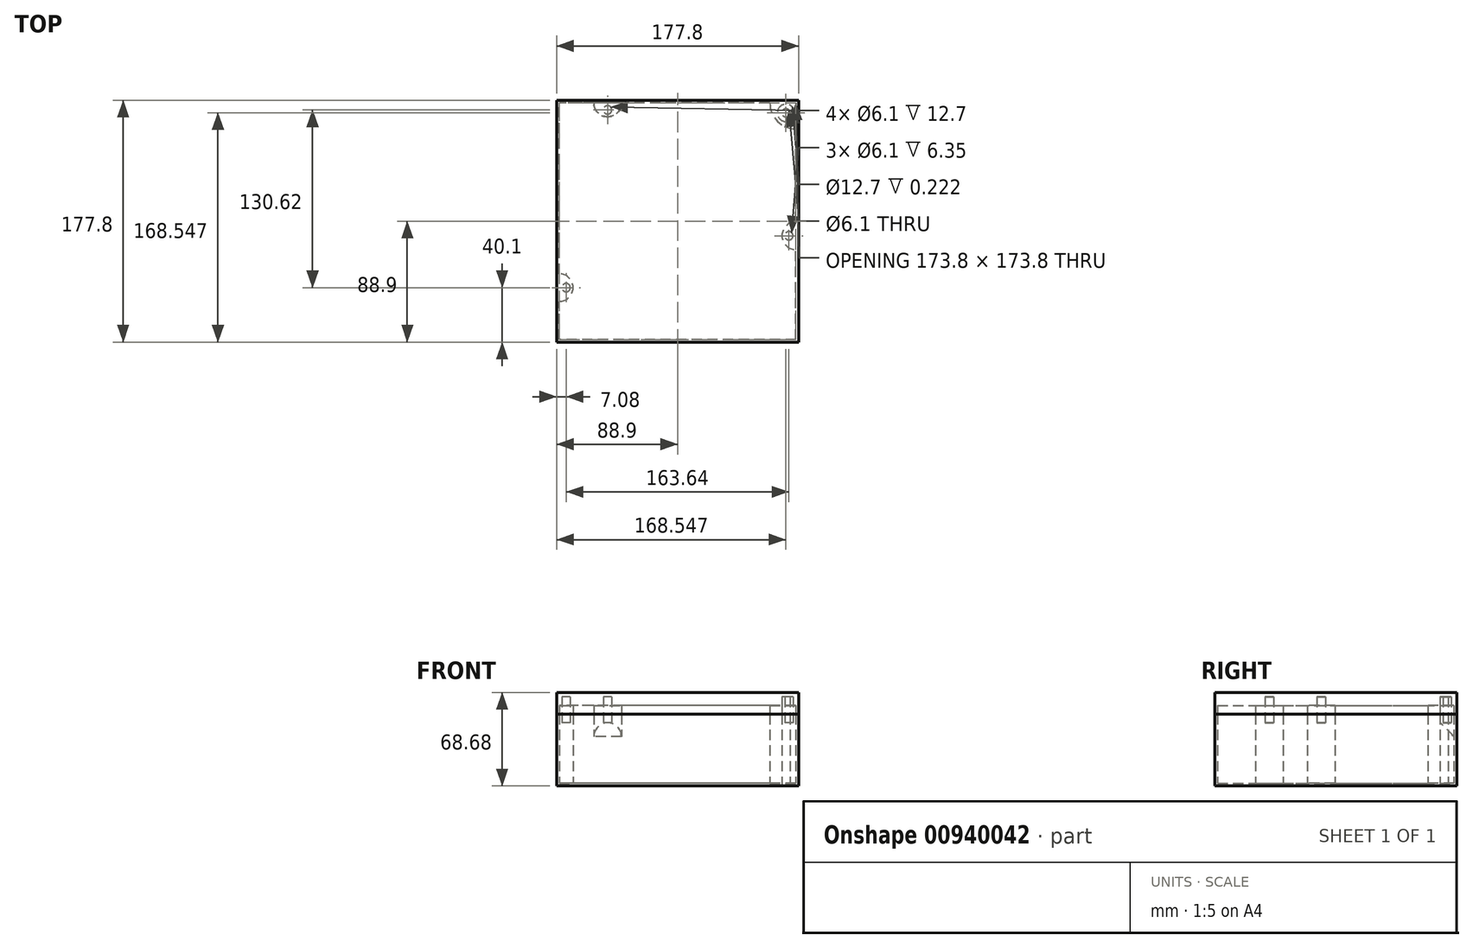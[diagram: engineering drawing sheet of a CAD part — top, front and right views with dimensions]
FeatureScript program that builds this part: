
annotation { "Feature Type Name" : "Feature", "Feature Type Description" : "" }
export const myFeature = defineFeature(function(context is Context, id is Id, definition is map)
    precondition{}
    {
        {
            var Q0;
            Q0=qCreatedBy(makeId("Top.planeOp"),FACE);
            var sketch = newSketch(context, id + "F0", { "sketchPlane" : qUnion([Q0])});
            skLineSegment(sketch, "E0.bottom", {"start": v(88.9, -88.9) * mm, "end": v(-88.9, -88.9) * mm});
            skLineSegment(sketch, "E0.top", {"start": v(88.9, 88.9) * mm, "end": v(-88.9, 88.9) * mm});
            skLineSegment(sketch, "E0.left", {"start": v(88.9, -88.9) * mm, "end": v(88.9, 88.9) * mm});
            skLineSegment(sketch, "E0.right", {"start": v(-88.9, -88.9) * mm, "end": v(-88.9, 88.9) * mm});
            skPoint(sketch, "E0.middle", {"position": v(0, 0) * mm});
            skSolve(sketch);
        }
        {
            var Q0;
            Q0=makeQuery(id+"F0.imprint","IMPRINT",FACE,{"disambiguationData":[TD([[makeQuery(id+"F0.imprint","IMPRINT",EDGE,{"derivedFrom":sQuery(id+"F0.wireOp",EDGE,"E0.bottom")}),-1.0]])]});
            extrude(context, id + "F1", {"entities" : qUnion([Q0]), "depth" : 6.35 * mm, "offsetDistance" : 25 * mm});
        }
        {
            var Q0;
            Q0=makeQuery(id+"F1.opExtrude","CAP_FACE",FACE,{"disambiguationData":[OSD([sQuery(id+"F0.wireOp",EDGE,"E0.bottom"),sQuery(id+"F0.wireOp",EDGE,"E0.top"),sQuery(id+"F0.wireOp",EDGE,"E0.left"),sQuery(id+"F0.wireOp",EDGE,"E0.right")])],"isStart":false});
            var sketch = newSketch(context, id + "F2", { "sketchPlane" : qUnion([Q0])});
            skLineSegment(sketch, "E1.bottom", {"start": v(86.9, -86.9) * mm, "end": v(-86.9, -86.9) * mm});
            skLineSegment(sketch, "E1.top", {"start": v(67.85, 86.9) * mm, "end": v(-41.18, 86.9) * mm});
            skLineSegment(sketch, "E1.left", {"start": v(86.9, -86.9) * mm, "end": v(86.9, -20.86) * mm});
            skLineSegment(sketch, "E1.right", {"start": v(-86.9, -86.9) * mm, "end": v(-86.9, -58.96) * mm});
            skPoint(sketch, "E1.middle", {"position": v(0, 0) * mm});
            skArc(sketch, "E2", {"start": v(-86.9, -58.96) * mm, "mid": v(-76.74, -48.8) * mm, "end": v(-86.9, -38.64) * mm});
            skArc(sketch, "E3", {"start": v(86.9, -0.54) * mm, "mid": v(76.74, -10.7) * mm, "end": v(86.9, -20.86) * mm});
            skArc(sketch, "E4", {"start": v(-61.5, 86.9) * mm, "mid": v(-51.34, 76.74) * mm, "end": v(-41.18, 86.9) * mm});
            skArc(sketch, "E5", {"start": v(67.85, 86.9) * mm, "mid": v(73.43, 73.43) * mm, "end": v(86.9, 67.85) * mm});
            skPoint(sketch, "E6.orphan", {"position": v(-51.34, 76.74) * mm});
            skLineSegment(sketch, "E7.trimOffspring", {"start": v(-61.5, 86.9) * mm, "end": v(-86.9, 86.9) * mm});
            skPoint(sketch, "E8.orphan", {"position": v(-76.74, -48.8) * mm});
            skLineSegment(sketch, "E9.trimOffspring", {"start": v(-86.9, -38.64) * mm, "end": v(-86.9, 86.9) * mm});
            skCircle(sketch, "E10", {"center": v(81.82, -10.7) * mm, "radius": 3.05 * mm});
            skLineSegment(sketch, "E11.trimOffspring", {"start": v(86.9, -0.54) * mm, "end": v(86.9, 67.85) * mm});
            skLineSegment(sketch, "E12", {"start": v(-86.9, 86.9) * mm, "end": v(-61.5, 86.9) * mm});
            skLineSegment(sketch, "E13.trimOffspring", {"start": v(-41.18, 86.9) * mm, "end": v(67.85, 86.9) * mm});
            skCircle(sketch, "E14", {"center": v(79.65, 79.65) * mm, "radius": 3.05 * mm});
            skLineSegment(sketch, "E15", {"start": v(86.9, -10.7) * mm, "end": v(76.74, -10.7) * mm});
            skCircle(sketch, "E16", {"center": v(-51.34, 81.82) * mm, "radius": 3.05 * mm});
            skCircle(sketch, "E17", {"center": v(-81.82, -48.8) * mm, "radius": 3.05 * mm});
            skPoint(sketch, "E18.start.orphan", {"position": v(88.9, 88.9) * mm});
            skSolve(sketch);
        }
        {
            var Q0;
            Q0=makeQuery(id+"F2.imprint","IMPRINT",FACE,{"disambiguationData":[TD([[makeQuery(id+"F2.imprint","IMPRINT",EDGE,{"derivedFrom":sQuery(id+"F2.wireOp",EDGE,"E1.bottom")}),1.0]])]});
            extrude(context, id + "F3", {"entities" : qUnion([Q0]), "operationType" : NewBodyOperationType.ADD, "depth" : 50.8 * mm, "offsetDistance" : 25.4 * mm});
        }
        {
            var Q0;
            Q0=makeQuery(id+"F3.boolean.opBoolean","SPLIT",FACE,{"disambiguationData":[TD([makeQuery(id+"F3.opExtrude","SWEPT_FACE",FACE,{"disambiguationData":[OSD([sQuery(id+"F2.wireOp",EDGE,"E16")])]})])],"derivedFrom":makeQuery(id+"F1.opExtrude","CAP_FACE",FACE,{"disambiguationData":[OSD([sQuery(id+"F0.wireOp",EDGE,"E0.bottom"),sQuery(id+"F0.wireOp",EDGE,"E0.top"),sQuery(id+"F0.wireOp",EDGE,"E0.left"),sQuery(id+"F0.wireOp",EDGE,"E0.right")])],"isStart":false})});
            var Q1;
            Q1=makeQuery(id+"F3.boolean.opBoolean","SPLIT",FACE,{"disambiguationData":[TD([makeQuery(id+"F3.opExtrude","SWEPT_FACE",FACE,{"disambiguationData":[OSD([sQuery(id+"F2.wireOp",EDGE,"E10")])]})])],"derivedFrom":makeQuery(id+"F1.opExtrude","CAP_FACE",FACE,{"disambiguationData":[OSD([sQuery(id+"F0.wireOp",EDGE,"E0.bottom"),sQuery(id+"F0.wireOp",EDGE,"E0.top"),sQuery(id+"F0.wireOp",EDGE,"E0.left"),sQuery(id+"F0.wireOp",EDGE,"E0.right")])],"isStart":false})});
            var Q2;
            Q2=makeQuery(id+"F3.boolean.opBoolean","SPLIT",FACE,{"disambiguationData":[TD([makeQuery(id+"F3.opExtrude","SWEPT_FACE",FACE,{"disambiguationData":[OSD([sQuery(id+"F2.wireOp",EDGE,"E17")])]})])],"derivedFrom":makeQuery(id+"F1.opExtrude","CAP_FACE",FACE,{"disambiguationData":[OSD([sQuery(id+"F0.wireOp",EDGE,"E0.bottom"),sQuery(id+"F0.wireOp",EDGE,"E0.top"),sQuery(id+"F0.wireOp",EDGE,"E0.left"),sQuery(id+"F0.wireOp",EDGE,"E0.right")])],"isStart":false})});
            extrude(context, id + "F4", {"entities" : qUnion([Q0, Q1, Q2]), "operationType" : NewBodyOperationType.ADD, "depth" : 44.45 * mm, "offsetDistance" : 25.4 * mm});
        }
        {
            var Q0;
            Q0=makeQuery(id+"F3.boolean.opBoolean","SPLIT",FACE,{"disambiguationData":[TD([makeQuery(id+"F3.opExtrude","SWEPT_FACE",FACE,{"disambiguationData":[OSD([sQuery(id+"F2.wireOp",EDGE,"E14")])]})])],"derivedFrom":makeQuery(id+"F1.opExtrude","CAP_FACE",FACE,{"disambiguationData":[OSD([sQuery(id+"F0.wireOp",EDGE,"E0.bottom"),sQuery(id+"F0.wireOp",EDGE,"E0.top"),sQuery(id+"F0.wireOp",EDGE,"E0.left"),sQuery(id+"F0.wireOp",EDGE,"E0.right")])],"isStart":false})});
            extrude(context, id + "F5", {"entities" : qUnion([Q0]), "operationType" : NewBodyOperationType.REMOVE, "oppositeDirection" : true, "depth" : 12.75 * mm, "offsetDistance" : 25.4 * mm});
        }
        {
            var Q0;
            Q0=makeQuery(id+"F1.opExtrude","CAP_FACE",FACE,{"disambiguationData":[OSD([sQuery(id+"F0.wireOp",EDGE,"E0.bottom"),sQuery(id+"F0.wireOp",EDGE,"E0.top"),sQuery(id+"F0.wireOp",EDGE,"E0.left"),sQuery(id+"F0.wireOp",EDGE,"E0.right")])],"isStart":true});
            var sketch = newSketch(context, id + "F6", { "sketchPlane" : qUnion([Q0])});
            skCircle(sketch, "E19", {"center": v(79.65, -79.65) * mm, "radius": 6.35 * mm});
            skSolve(sketch);
        }
        {
            var Q0;
            Q0=makeQuery(id+"F6.imprint","IMPRINT",FACE,{"disambiguationData":[TD([[makeQuery(id+"F6.imprint","IMPRINT",EDGE,{"derivedFrom":sQuery(id+"F6.wireOp",EDGE,"E19")}),1.0]])]});
            extrude(context, id + "F7", {"entities" : qUnion([Q0]), "operationType" : NewBodyOperationType.REMOVE, "oppositeDirection" : true, "depth" : 4.57 * mm, "offsetDistance" : 25.4 * mm});
        }
        {
            var Q0;
            Q0=makeQuery(id+"F3.opExtrude","CAP_FACE",FACE,{"disambiguationData":[OSD([sQuery(id+"F0.wireOp",EDGE,"E0.bottom"),sQuery(id+"F0.wireOp",EDGE,"E0.top"),sQuery(id+"F0.wireOp",EDGE,"E0.left"),sQuery(id+"F0.wireOp",EDGE,"E0.right"),sQuery(id+"F2.wireOp",EDGE,"E1.bottom"),sQuery(id+"F2.wireOp",EDGE,"E1.left"),sQuery(id+"F2.wireOp",EDGE,"E1.right"),sQuery(id+"F2.wireOp",EDGE,"E2"),sQuery(id+"F2.wireOp",EDGE,"E3"),sQuery(id+"F2.wireOp",EDGE,"E4"),sQuery(id+"F2.wireOp",EDGE,"E5"),sQuery(id+"F2.wireOp",EDGE,"SM7KM1Kk-73DD-m9rY-A4iJ-MEBE9odaTNSM"),sQuery(id+"F2.wireOp",EDGE,"twTWXflB-vlQ6-LPMN-hA2H-3E9qFKBzkKEc"),sQuery(id+"F2.wireOp",EDGE,"E9.trimOffspring"),sQuery(id+"F2.wireOp",EDGE,"E10"),sQuery(id+"F2.wireOp",EDGE,"E11.trimOffspring"),sQuery(id+"F2.wireOp",EDGE,"E12"),sQuery(id+"F2.wireOp",EDGE,"E13.trimOffspring"),sQuery(id+"F2.wireOp",EDGE,"E14")])],"isStart":false});
            var sketch = newSketch(context, id + "F8", { "sketchPlane" : qUnion([Q0])});
            skLineSegment(sketch, "E20.0.0", {"start": v(-88.9, -88.9) * mm, "end": v(88.9, -88.9) * mm});
            skLineSegment(sketch, "E20.0.1", {"start": v(88.9, -88.9) * mm, "end": v(88.9, 88.9) * mm});
            skLineSegment(sketch, "E20.0.2", {"start": v(88.9, 88.9) * mm, "end": v(-88.9, 88.9) * mm});
            skLineSegment(sketch, "E20.0.3", {"start": v(-88.9, 88.9) * mm, "end": v(-88.9, -88.9) * mm});
            skArc(sketch, "E21.0", {"start": v(-61.5, 86.9) * mm, "mid": v(-51.34, 76.74) * mm, "end": v(-41.18, 86.9) * mm});
            skArc(sketch, "E22.0.0", {"start": v(-41.18, 86.9) * mm, "mid": v(-51.34, 76.74) * mm, "end": v(-61.5, 86.9) * mm});
            skLineSegment(sketch, "E22.0.1", {"start": v(-61.5, 86.9) * mm, "end": v(-86.9, 86.9) * mm});
            skLineSegment(sketch, "E22.0.2", {"start": v(-86.9, 86.9) * mm, "end": v(-86.9, -38.64) * mm});
            skArc(sketch, "E22.0.3", {"start": v(-86.9, -38.64) * mm, "mid": v(-76.74, -48.8) * mm, "end": v(-86.9, -58.96) * mm});
            skLineSegment(sketch, "E22.0.4", {"start": v(-86.9, -58.96) * mm, "end": v(-86.9, -86.9) * mm});
            skLineSegment(sketch, "E22.0.5", {"start": v(-86.9, -86.9) * mm, "end": v(86.9, -86.9) * mm});
            skLineSegment(sketch, "E22.0.6", {"start": v(86.9, -86.9) * mm, "end": v(86.9, -20.86) * mm});
            skArc(sketch, "E22.0.7", {"start": v(86.9, -20.86) * mm, "mid": v(76.74, -10.7) * mm, "end": v(86.9, -0.54) * mm});
            skLineSegment(sketch, "E22.0.8", {"start": v(86.9, -0.54) * mm, "end": v(86.9, 67.85) * mm});
            skArc(sketch, "E22.0.9", {"start": v(86.9, 67.85) * mm, "mid": v(73.43, 73.43) * mm, "end": v(67.85, 86.9) * mm});
            skLineSegment(sketch, "E22.0.10", {"start": v(67.85, 86.9) * mm, "end": v(-41.18, 86.9) * mm});
            skSolve(sketch);
        }
        {
            var Q0;
            Q0=makeQuery(id+"F8.imprint","IMPRINT",FACE,{"disambiguationData":[TD([[makeQuery(id+"F8.imprint","IMPRINT",EDGE,{"derivedFrom":sQuery(id+"F8.wireOp",EDGE,"E20.0.0")}),-1.0]])]});
            extrude(context, id + "F9", {"entities" : qUnion([Q0]), "depth" : 6.35 * mm, "offsetDistance" : 25.4 * mm});
        }
        {
            var Q0;
            Q0=makeQuery(id+"F9.opExtrude","CAP_FACE",FACE,{"disambiguationData":[OSD([sQuery(id+"F2.wireOp",EDGE,"SM7KM1Kk-73DD-m9rY-A4iJ-MEBE9odaTNSM"),sQuery(id+"F2.wireOp",EDGE,"twTWXflB-vlQ6-LPMN-hA2H-3E9qFKBzkKEc"),sQuery(id+"F2.wireOp",EDGE,"E10"),sQuery(id+"F2.wireOp",EDGE,"E14"),sQuery(id+"F8.wireOp",EDGE,"E20.0.0"),sQuery(id+"F8.wireOp",EDGE,"E20.0.1"),sQuery(id+"F8.wireOp",EDGE,"E20.0.2"),sQuery(id+"F8.wireOp",EDGE,"E20.0.3"),sQuery(id+"F8.wireOp",EDGE,"E22.0.0"),sQuery(id+"F8.wireOp",EDGE,"E22.0.1"),sQuery(id+"F8.wireOp",EDGE,"E22.0.2"),sQuery(id+"F8.wireOp",EDGE,"E22.0.3"),sQuery(id+"F8.wireOp",EDGE,"E22.0.4"),sQuery(id+"F8.wireOp",EDGE,"E22.0.5"),sQuery(id+"F8.wireOp",EDGE,"E22.0.6"),sQuery(id+"F8.wireOp",EDGE,"E22.0.7"),sQuery(id+"F8.wireOp",EDGE,"E22.0.8"),sQuery(id+"F8.wireOp",EDGE,"E22.0.9"),sQuery(id+"F8.wireOp",EDGE,"E22.0.10")])],"isStart":false});
            var sketch = newSketch(context, id + "F10", { "sketchPlane" : qUnion([Q0])});
            skLineSegment(sketch, "E23.0.0", {"start": v(-88.9, -88.9) * mm, "end": v(88.9, -88.9) * mm});
            skLineSegment(sketch, "E23.0.1", {"start": v(88.9, -88.9) * mm, "end": v(88.9, 88.9) * mm});
            skLineSegment(sketch, "E23.0.2", {"start": v(88.9, 88.9) * mm, "end": v(-88.9, 88.9) * mm});
            skLineSegment(sketch, "E23.0.3", {"start": v(-88.9, 88.9) * mm, "end": v(-88.9, -88.9) * mm});
            skSolve(sketch);
        }
        {
            var Q0;
            Q0 = qSketchRegion(id + "F10", true);
            extrude(context, id + "F11", {"entities" : qUnion([Q0]), "operationType" : NewBodyOperationType.ADD, "depth" : 9.52 * mm, "offsetDistance" : 25.4 * mm});
        }
        {
            var Q0;
            Q0=makeQuery(id+"F11.boolean.opBoolean","SPLIT",FACE,{"disambiguationData":[TD([makeQuery(id+"F9.opExtrude","SWEPT_FACE",FACE,{"disambiguationData":[OSD([sQuery(id+"F2.wireOp",EDGE,"E17")])]})])],"derivedFrom":makeQuery(id+"F11.opExtrude","CAP_FACE",FACE,{"disambiguationData":[OSD([sQuery(id+"F10.wireOp",EDGE,"E23.0.0"),sQuery(id+"F10.wireOp",EDGE,"E23.0.1"),sQuery(id+"F10.wireOp",EDGE,"E23.0.2"),sQuery(id+"F10.wireOp",EDGE,"E23.0.3")])],"isStart":true})});
            var Q1;
            Q1=makeQuery(id+"F11.boolean.opBoolean","SPLIT",FACE,{"disambiguationData":[TD([makeQuery(id+"F9.opExtrude","SWEPT_FACE",FACE,{"disambiguationData":[OSD([sQuery(id+"F2.wireOp",EDGE,"E10")])]})])],"derivedFrom":makeQuery(id+"F11.opExtrude","CAP_FACE",FACE,{"disambiguationData":[OSD([sQuery(id+"F10.wireOp",EDGE,"E23.0.0"),sQuery(id+"F10.wireOp",EDGE,"E23.0.1"),sQuery(id+"F10.wireOp",EDGE,"E23.0.2"),sQuery(id+"F10.wireOp",EDGE,"E23.0.3")])],"isStart":true})});
            var Q2;
            Q2=makeQuery(id+"F11.boolean.opBoolean","SPLIT",FACE,{"disambiguationData":[TD([makeQuery(id+"F9.opExtrude","SWEPT_FACE",FACE,{"disambiguationData":[OSD([sQuery(id+"F2.wireOp",EDGE,"E16")])]})])],"derivedFrom":makeQuery(id+"F11.opExtrude","CAP_FACE",FACE,{"disambiguationData":[OSD([sQuery(id+"F10.wireOp",EDGE,"E23.0.0"),sQuery(id+"F10.wireOp",EDGE,"E23.0.1"),sQuery(id+"F10.wireOp",EDGE,"E23.0.2"),sQuery(id+"F10.wireOp",EDGE,"E23.0.3")])],"isStart":true})});
            var Q3;
            Q3=makeQuery(id+"F11.boolean.opBoolean","SPLIT",FACE,{"disambiguationData":[TD([makeQuery(id+"F9.opExtrude","SWEPT_FACE",FACE,{"disambiguationData":[OSD([sQuery(id+"F2.wireOp",EDGE,"E14")])]})])],"derivedFrom":makeQuery(id+"F11.opExtrude","CAP_FACE",FACE,{"disambiguationData":[OSD([sQuery(id+"F10.wireOp",EDGE,"E23.0.0"),sQuery(id+"F10.wireOp",EDGE,"E23.0.1"),sQuery(id+"F10.wireOp",EDGE,"E23.0.2"),sQuery(id+"F10.wireOp",EDGE,"E23.0.3")])],"isStart":true})});
            extrude(context, id + "F12", {"entities" : qUnion([Q0, Q1, Q2, Q3]), "operationType" : NewBodyOperationType.REMOVE, "oppositeDirection" : true, "depth" : 6.35 * mm, "offsetDistance" : 25.4 * mm});
        }
        {
            var Q0;
            Q0=makeQuery(id+"F3.opExtrude","SWEPT_FACE",FACE,{"disambiguationData":[OSD([sQuery(id+"F2.wireOp",EDGE,"E9.trimOffspring")])]});
            var sketch = newSketch(context, id + "F13", { "sketchPlane" : qUnion([Q0])});
            skLineSegment(sketch, "E24.0", {"start": v(86.9, 57.15) * mm, "end": v(86.9, 6.35) * mm});
            skLineSegment(sketch, "E25.0", {"start": v(-86.9, 57.15) * mm, "end": v(-86.9, 6.35) * mm});
            skLineSegment(sketch, "E26", {"start": v(86.9, 40.67) * mm, "end": v(72.48, 55.1) * mm});
            skLineSegment(sketch, "E27.0.0", {"start": v(-38.64, 6.35) * mm, "end": v(86.9, 6.35) * mm});
            skLineSegment(sketch, "E27.0.1", {"start": v(86.9, 6.35) * mm, "end": v(86.9, 57.15) * mm});
            skLineSegment(sketch, "E27.0.2", {"start": v(86.9, 57.15) * mm, "end": v(-38.64, 57.15) * mm});
            skLineSegment(sketch, "E27.0.3", {"start": v(-38.64, 57.15) * mm, "end": v(-38.64, 6.35) * mm});
            skLineSegment(sketch, "E28", {"start": v(72.48, 55.1) * mm, "end": v(72.48, 6.35) * mm});
            skLineSegment(sketch, "E29.0.0", {"start": v(78.77, 50.8) * mm, "end": v(84.87, 50.8) * mm});
            skPoint(sketch, "E30", {"position": v(78.77, 48.8) * mm});
            skLineSegment(sketch, "E31", {"start": v(86.9, 40.67) * mm, "end": v(86.9, 6.35) * mm});
            skLineSegment(sketch, "E32.MirrorCS", {"start": v(-78.77, 50.8) * mm, "end": v(-84.87, 50.8) * mm});
            skLineSegment(sketch, "E33.MirrorCS", {"start": v(-86.9, 40.67) * mm, "end": v(-86.9, 6.35) * mm});
            skLineSegment(sketch, "E34.MirrorCS", {"start": v(-72.48, 55.1) * mm, "end": v(-72.48, 6.35) * mm});
            skPoint(sketch, "E35.MirrorP", {"position": v(-78.77, 48.8) * mm});
            skLineSegment(sketch, "E36.MirrorCS", {"start": v(-86.9, 40.67) * mm, "end": v(-72.48, 55.1) * mm});
            skLineSegment(sketch, "E37.MirrorCS", {"start": v(-86.9, 6.35) * mm, "end": v(-86.9, 57.15) * mm});
            skLineSegment(sketch, "E38.0", {"start": v(-86.9, 6.35) * mm, "end": v(-58.96, 6.35) * mm});
            skLineSegment(sketch, "E39", {"start": v(0, 0) * mm, "end": v(0, 102.14) * mm, "construction": true});
            skSolve(sketch);
        }
        {
            var Q0;
            Q0=makeQuery(id+"F13.imprint","IMPRINT",FACE,{"disambiguationData":[TD([[makeQuery(id+"F13.imprint","IMPRINT",EDGE,{"derivedFrom":sQuery(id+"F13.wireOp",EDGE,"E26")}),1.0]])]});
            var Q1;
            {var subQ0=sQuery(id+"F13.wireOp",EDGE,"E34.MirrorCS");Q1=makeQuery(id+"F13.imprint","IMPRINT",FACE,{"disambiguationData":[TD([[makeQuery(id+"F13.imprint","IMPRINT",EDGE,{"derivedFrom":subQ0}),-1.0]])]});}
            extrude(context, id + "F14", {"entities" : qUnion([Q0, Q1]), "operationType" : NewBodyOperationType.REMOVE, "depth" : 88.9 * mm, "offsetDistance" : 25.4 * mm});
        }
        {
            var Q0;
            Q0=qCreatedBy(makeId("Right.planeOp"),FACE);
            var sketch = newSketch(context, id + "F15", { "sketchPlane" : qUnion([Q0])});
            skLineSegment(sketch, "E40", {"start": v(0, 0) * mm, "end": v(0, 86.56) * mm, "construction": true});
            skSolve(sketch);
        }
        {
            var Q0;
            {var subQ0=sQuery(id+"F0.wireOp",EDGE,"E0.bottom");Q0=makeQuery(id+"F3.boolean.opBoolean","MERGE",FACE,{"derivedFrom":[makeQuery(id+"F1.opExtrude","SWEPT_FACE",FACE,{"disambiguationData":[OSD([subQ0])]}),makeQuery(id+"F3.opExtrude","SWEPT_FACE",FACE,{"disambiguationData":[OSD([subQ0])]})]});}
            var sketch = newSketch(context, id + "F16", { "sketchPlane" : qUnion([Q0])});
            skLineSegment(sketch, "E41.0.0", {"start": v(-88.9, 0) * mm, "end": v(88.9, 0) * mm});
            skLineSegment(sketch, "E41.0.1", {"start": v(88.9, 0) * mm, "end": v(88.9, 57.15) * mm});
            skLineSegment(sketch, "E41.0.2", {"start": v(88.9, 57.15) * mm, "end": v(-88.9, 57.15) * mm});
            skLineSegment(sketch, "E41.0.3", {"start": v(-88.9, 57.15) * mm, "end": v(-88.9, 0) * mm});
            skLineSegment(sketch, "E42.top", {"start": v(-88.9, 4.35) * mm, "end": v(88.9, 4.35) * mm});
            skLineSegment(sketch, "E42.left", {"start": v(-88.9, 0) * mm, "end": v(-88.9, 4.35) * mm});
            skLineSegment(sketch, "E42.right", {"start": v(88.9, 0) * mm, "end": v(88.9, 4.35) * mm});
            skLineSegment(sketch, "E43.0.0", {"start": v(67.85, 6.35) * mm, "end": v(-86.9, 6.35) * mm});
            skLineSegment(sketch, "E43.0.2", {"start": v(-86.9, 6.35) * mm, "end": v(86.9, 6.35) * mm});
            skLineSegment(sketch, "E43.0.4", {"start": v(86.9, 6.35) * mm, "end": v(67.85, 6.35) * mm});
            skSolve(sketch);
        }
        {
            var Q0;
            Q0=makeQuery(id+"F16.imprint","IMPRINT",FACE,{"disambiguationData":[TD([[makeQuery(id+"F16.imprint","IMPRINT",EDGE,{"derivedFrom":sQuery(id+"F16.wireOp",EDGE,"E41.0.0")}),-1.0]])]});
            extrude(context, id + "F17", {"entities" : qUnion([Q0]), "operationType" : NewBodyOperationType.REMOVE, "endBound" : BoundingType.UP_TO_NEXT, "oppositeDirection" : true, "depth" : 25.4 * mm, "offsetDistance" : 25.4 * mm});
        }
    });
